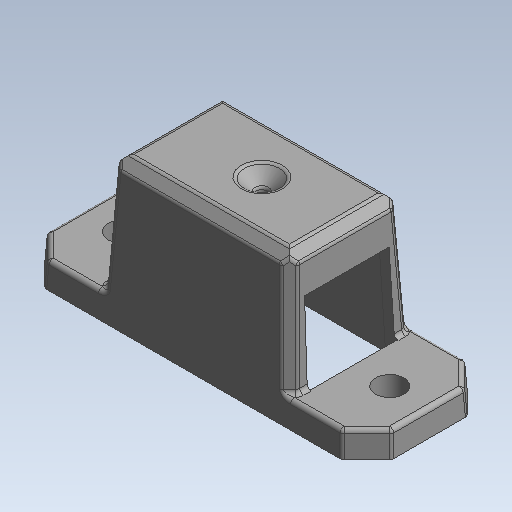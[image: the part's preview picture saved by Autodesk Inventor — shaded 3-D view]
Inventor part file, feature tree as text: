
AUTODESK INVENTOR PART (.ipt)
format: ipt  version: 2020 (Build 240168000, 168)  size: 628,736 bytes
history: native  units: mm (DEFAULTED — no unit token found)
features: fillet x1
ambient origin geometry x8: Origin, YZ Plane, XZ Plane, XY Plane, X Axis, Y Axis, Z Axis, Center Point
bodies: Solid1 (feature_tree)
feature tree (1):
  fillet  "Fillet5"  [1 undecoded]
note: 1 required parameter value undecoded (feature->parameter linkage not recoverable at this tier; creation-order binding heuristic only, values carry confidence <= 0.55)
